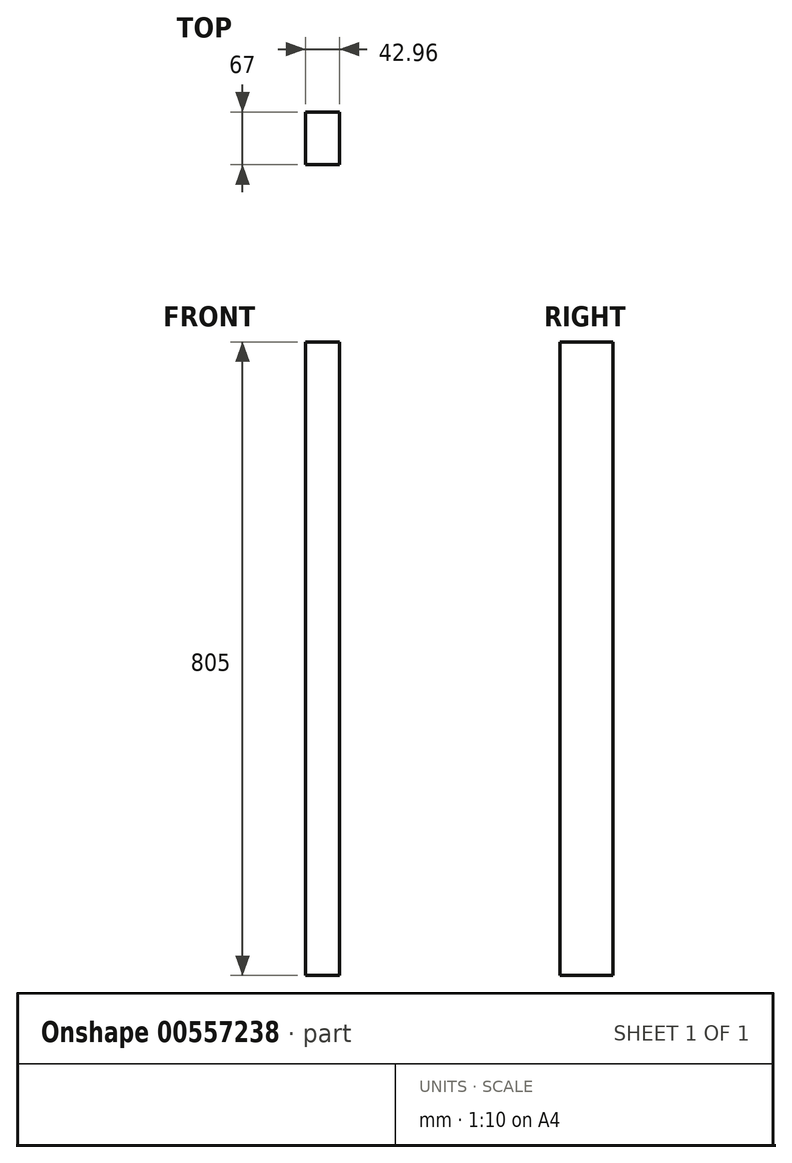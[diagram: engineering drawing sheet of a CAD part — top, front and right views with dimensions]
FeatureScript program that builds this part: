
annotation { "Feature Type Name" : "Feature", "Feature Type Description" : "" }
export const myFeature = defineFeature(function(context is Context, id is Id, definition is map)
    precondition{}
    {
        {
            var Q0;
            Q0=qCreatedBy(makeId("Top.planeOp"),FACE);
            var sketch = newSketch(context, id + "F0", { "sketchPlane" : qUnion([Q0])});
            skLineSegment(sketch, "E0.bottom", {"start": v(0, 0) * mm, "end": v(42.96, 0) * mm});
            skLineSegment(sketch, "E0.top", {"start": v(0, -67) * mm, "end": v(42.96, -67) * mm});
            skLineSegment(sketch, "E0.left", {"start": v(0, 0) * mm, "end": v(0, -67) * mm});
            skLineSegment(sketch, "E0.right", {"start": v(42.96, 0) * mm, "end": v(42.96, -67) * mm});
            skSolve(sketch);
        }
        {
            var Q0;
            Q0=makeQuery(id+"F0.imprint","IMPRINT",FACE,{"disambiguationData":[TD([[makeQuery(id+"F0.imprint","IMPRINT",EDGE,{"derivedFrom":sQuery(id+"F0.wireOp",EDGE,"E0.bottom")}),-1.0]])]});
            extrude(context, id + "F1", {"entities" : qUnion([Q0]), "depth" : 780 * mm, "offsetDistance" : 25 * mm});
        }
        {
            var Q0;
            Q0=makeQuery(id+"F1.opExtrude","CAP_FACE",FACE,{"disambiguationData":[OSD([sQuery(id+"F0.wireOp",EDGE,"E0.bottom"),sQuery(id+"F0.wireOp",EDGE,"E0.top"),sQuery(id+"F0.wireOp",EDGE,"E0.left"),sQuery(id+"F0.wireOp",EDGE,"E0.right")])],"isStart":false});
            extrude(context, id + "F2", {"entities" : qUnion([Q0]), "operationType" : NewBodyOperationType.ADD, "depth" : 25 * mm, "offsetDistance" : 25 * mm});
        }
    });
